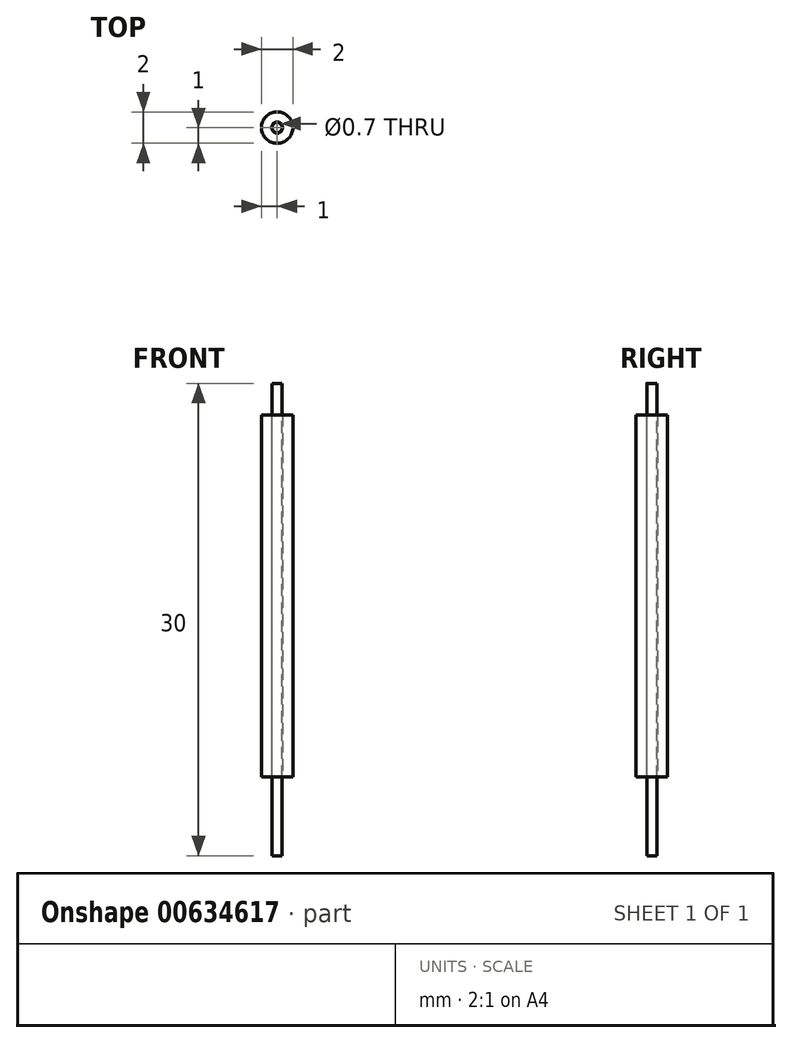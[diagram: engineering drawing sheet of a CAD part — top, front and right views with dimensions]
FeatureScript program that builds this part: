
annotation { "Feature Type Name" : "Feature", "Feature Type Description" : "" }
export const myFeature = defineFeature(function(context is Context, id is Id, definition is map)
    precondition{}
    {
        {
            var Q0;
            Q0=qCreatedBy(makeId("Front.planeOp"),FACE);
            var sketch = newSketch(context, id + "F0", { "sketchPlane" : qUnion([Q0])});
            skLineSegment(sketch, "E0.bottom", {"start": v(0, 0) * mm, "end": v(-0.32, 0) * mm});
            skLineSegment(sketch, "E0.top", {"start": v(0, 0) * mm, "end": v(-0.32, 0) * mm});
            skLineSegment(sketch, "E0.left", {"start": v(0, 0) * mm, "end": v(0, 0) * mm});
            skLineSegment(sketch, "E0.right", {"start": v(-0.32, 0) * mm, "end": v(-0.32, 0) * mm});
            skLineSegment(sketch, "E1.bottom", {"start": v(0, 30) * mm, "end": v(-0.32, 30) * mm});
            skLineSegment(sketch, "E1.left", {"start": v(0, 30) * mm, "end": v(0, 0) * mm});
            skLineSegment(sketch, "E1.right", {"start": v(-0.32, 30) * mm, "end": v(-0.32, 0) * mm});
            skSolve(sketch);
        }
        {
            var Q0;
            Q0=qSketchRegion(id+"F0",true);
            var Q1;
            Q1=sQuery(id+"F0.wireOp",EDGE,"E1.left");
            revolve(context, id + "F1", {"entities" : qUnion([Q0]), "axis" : qUnion([Q1]), "revolveType" : RevolveType.FULL});
        }
        {
            var Q0;
            Q0=qCreatedBy(makeId("Front.planeOp"),FACE);
            var sketch = newSketch(context, id + "F2", { "sketchPlane" : qUnion([Q0])});
            skLineSegment(sketch, "E2.bottom", {"start": v(-0.35, 5) * mm, "end": v(-1, 5) * mm});
            skLineSegment(sketch, "E2.top", {"start": v(-0.35, 28) * mm, "end": v(-1, 28) * mm});
            skLineSegment(sketch, "E2.left", {"start": v(-0.35, 5) * mm, "end": v(-0.35, 28) * mm});
            skLineSegment(sketch, "E2.right", {"start": v(-1, 5) * mm, "end": v(-1, 28) * mm});
            skLineSegment(sketch, "E3", {"start": v(0, 0) * mm, "end": v(0, 37.8) * mm});
            skSolve(sketch);
        }
        {
            var Q0;
            Q0=qSketchRegion(id+"F2",true);
            var Q1;
            Q1=sQuery(id+"F2.wireOp",EDGE,"E3");
            revolve(context, id + "F3", {"operationType" : NewBodyOperationType.ADD, "entities" : qUnion([Q0]), "axis" : qUnion([Q1]), "revolveType" : RevolveType.FULL});
        }
    });
